# Revit family: Domotics-DomesticRanges-GEWISS-CHORUS_DATA-CONNECTOR_SOUND_DIFFUSION
name_source: partatom
category: Apparecchi elettrici
revit_build: Autodesk Revit 2016 (Build: 20161004_0715(x64)
units: mm (PartAtom-declared; Revit-internal decimal feet)

## family parameters
Condiviso = Sì
Host = Superficie
Mantenere orientamento annotazione = Sì
Punto di calcolo locali = Sì
Quota connettore circolare = Usa diametro
Taglio con vuoti quando caricato = No
Tipo di parte = Normale

## types (3) — shared parameters
Catalogue = DOMOTICS
Catalogue Range = CHORUS - SERIE CIVILE
Category = Connector
Description. = Connector
Description: = Speaker socket
Electrocod = 3720
IDF = 15f7e504-9186-4f21-a449-3aed8e615ebe
IDT = 1f108502-4920-4050-8423-f62229f2752f
Immagine tipo = GW14458.jpg
No. Chorus modules: = 1
Produttore = GEWISS S.p.A.
Prospetto di default = 1219 mm
SEO = Socket outlet
Technical sheet = https://www.gewiss.com
Tipo = CONNETTORE DIFFUSIONE SONORA : titanio
URL = https://www.gewiss.com
Version file RFA = 19.0
fronte = titanio
struttura = Default

## per-type parameters (varying)
| type | Colour | Descrizione | EAN code | Modello |
| GW10458 - SOUND DIFFUSION CONNECTOR WHITE | White | SOUND DIFFUSION CONNECTOR WHITE | 8011564719200 | GW10458 |
| GW14458 - SOUND DIFFUSION CONNECTOR TITANIUM | Titanium | SOUND DIFFUSION CONNECTOR TITANIUM | 8011564719262 | GW14458 |
| GW12458 - SOUND DIFFUSION CONNECTOR BLACK | Black | SOUND DIFFUSION CONNECTOR BLACK | 8011564719231 | GW12458 |

## geometry (parser evidence)
native form markers: Sweep x1
no freeform markers — native parametric forms only
